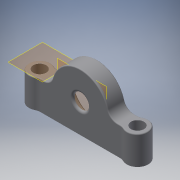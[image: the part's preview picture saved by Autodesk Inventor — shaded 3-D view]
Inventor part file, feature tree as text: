
AUTODESK INVENTOR PART (.ipt)
format: ipt  version: 2016 (Build 200138000, 138)  size: 207,872 bytes
history: native  units: in
note: dims shown in document units (in); Inventor stores cm internally (conversion verified against a paired STEP export)
features: plane x4, fillet x4, sketch x3, extrude x3, projected_geometry x3, reference x2, chamfer x1
ambient origin geometry x8: Origin, YZ Plane, XZ Plane, XY Plane, X Axis, Y Axis, Z Axis, Center Point
bodies: Solid1 (feature_tree)
feature tree (20):
  plane  "Work Plane1"
  sketch  "Sketch1"  dims[d0=0.0025in d1=0.25in d2=0.75in]
  plane  "Work Plane2"
  plane  "Work Plane4"
  extrude  "Extrusion1"  Depth=0.25in
  fillet  "Fillet1"  Radius=0.75in
  extrude  "Extrusion2"  Depth=0.25in
  fillet  "Fillet2"  Radius=0.05in
  fillet  "Fillet4"  Radius=0.05in
  chamfer  "Chamfer1"  Distance=0.0625in
  plane  "Work Plane3"
  extrude  "Extrusion3"  Depth=0.05in TaperAngle=45.0deg
  fillet  "Fillet6"  Radius=0.325in
  reference  "Reference1"
  sketch  "Sketch2"  dims[d3=1.0in d4=0.0in d5=0.25in d6=0.05in d7=0.05in d8=0.0in]
  projected_geometry  "Projected Loop1"
  reference  "Reference2"
  sketch  "Sketch3"  dims[d9=0.125in d11=0.0625in d12=0.05in d13=0.125in d14=45.0deg d15=0.325in d18=0.05in d19=0.0in d20=0.12in d21=0.12in d25=0.025in]
  projected_geometry  "Projected Loop2"
  projected_geometry  "Projected Loop3"
